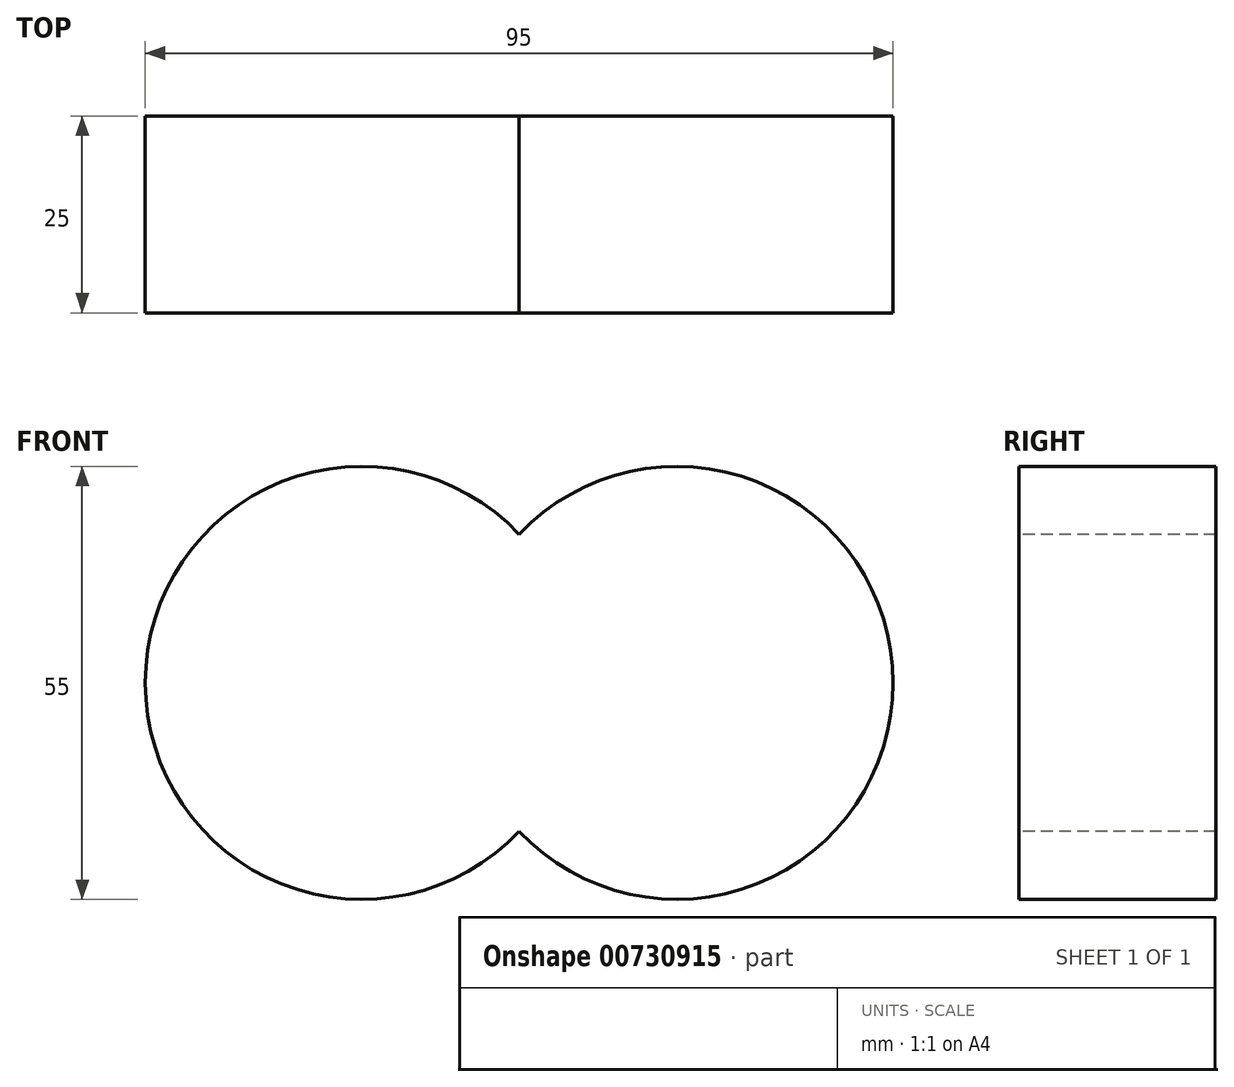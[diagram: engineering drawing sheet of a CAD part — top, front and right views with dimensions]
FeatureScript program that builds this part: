
annotation { "Feature Type Name" : "Feature", "Feature Type Description" : "" }
export const myFeature = defineFeature(function(context is Context, id is Id, definition is map)
    precondition{}
    {
        {
            var Q0;
            Q0=qCreatedBy(makeId("Front.planeOp"),FACE);
            var sketch = newSketch(context, id + "F0", { "sketchPlane" : qUnion([Q0])});
            skArc(sketch, "E0", {"start": v(0, 18.87) * mm, "mid": v(-47.5, 0) * mm, "end": v(0, -18.87) * mm});
            skArc(sketch, "E1", {"start": v(0, -18.87) * mm, "mid": v(47.5, 0) * mm, "end": v(0, 18.87) * mm});
            skSolve(sketch);
        }
        {
            var Q0;
            Q0 = qSketchRegion(id + "F0", true);
            extrude(context, id + "F1", {"entities" : qUnion([Q0]), "oppositeDirection" : true, "depth" : 25 * mm, "offsetDistance" : 25 * mm});
        }
    });
